# Revit family: 6185
name_source: partatom
category: Lighting Fixtures
revit_build: Autodesk Revit 2018 (Build: 20170223_1515(x64)
units: mm (PartAtom-declared; Revit-internal decimal feet)

## family parameters
Cut with Voids When Loaded = No
Host = Face
Light Source = Yes
OmniClass Number = 23.80.70.00
OmniClass Title = Lighting
Part Type = Normal
Room Calculation Point = No
Round Connector Dimension = Use Diameter
Shared = No

## types (1)
- 0006185 PIXO MINI PENDANT 490LM 927 MB WHT
    Apparent Load = 7 VA
    Assembly Code = D5020200
    AssetType = Fixed
    ClassificationName = Uniclass2015
    ClassificationValue = EF_70_80
    Color Filter = 16777215
    Cost = 0 $
    Cutout = 1200 mm
    Default Elevation = 1219 mm
    Description = Integrated LED pendant, Textured White - RAL9016, simple and slick integral design with no driver box and without any visible screws, ideal for retail applications, die-cast aluminium body, passive cooling heatsink. Beam angle: 40°, color temperature: 2700K , total system power: 6.5W, total fixture output: 490 lm, LOR: 100%, colour rendering: Ra: 90 typical, IR/UV free light source without heat radiation, operating voltage: 220-240V / 50-60Hz, electronic driver, non-dimmable, low LED flickerering rate (6%-20%), power factor: >0.90, electrical protection: Class I, Surface mounting ceiling rose, ingress protection rating: IP20, suitable for internal environment only, horizontal rotation: 345°, vertical tilt: 90°, dimensions: Ø41.5x350, weight: 0.469kg.
    Dimming Lamp Color Temperature Shift = <None>
    DocumentationLiterature = http://www.sylvania-lighting.com
    DurationUnit = hours
    ElectricShockClassification = 75
    Emit Shape Visible in Rendering = No
    Emit from Circle Diameter = 610 mm
    ExpectedLife = 50000
    Height = 51 mm
    IfcExportAs = Class I
    IfcExportType = IfcLightFixtureType
    ImpactProtectionIndex = IfcLightFixtureType
    IngressProtection = IfcLightFixtureType
    InputNominalFrequency = 2700
    InputVoltage = 0
    LampColourRenderingIndex = 16500
    LampColourTemperature = LED
    LampMacAdamStep = 90
    LampNominalLuminous = 2700 K
    Length = 1196 mm  [stored 3.92388 ft]
    LightOutputRatio = LED
    LuminaireType = 0
    ManufacturerName = 75 lm/W
    Material = Feilo Sylvania
    Material_1_FEILO = <By Category>
    Material_2_FEILO = <By Category>
    Material_3_FEILO = <By Category>
    Material_4_FEILO = <By Category>
    Model = Pixo Mini PENDANT 490lm 927 MB WHITE
    ModelNumber = 0006185
    ModelReference = Pixo Mini PENDANT 490lm 927 MB WHITE
    Name = Pixo Mini PENDANT 490lm 927 MB WHITE
    NominalDepth = 0 mm  [stored 0 ft]
    NominalHeight = 0 mm  [stored 0 ft]
    NominalLength = 85 mm
    Photometric Web File = 0006185.ies
    PowerConsumption = Lighting
    PowerFactor = 0
    Tilt Angle = 90.00°
    Type Image = <None>
    TypeName = Pixo Mini PENDANT 490lm 927 MB WHITE
    URL = 0.5
    Voltage = 0 V
    WarrantyDescription = http://www.sylvania-lighting.com
    Width = 296 mm  [stored 0.971129 ft]
    cutout width = 300 mm
    spacer centres = 1000 mm  [stored 3.28084 ft]
    spacer height = 6 mm  [stored 0.019685 ft]

note: [stored X ft] marks values corroborated as IEEE doubles in the binary element streams (Revit-internal decimal feet)

## geometry (parser evidence)
native form markers: Sweep x1
no freeform markers — native parametric forms only
